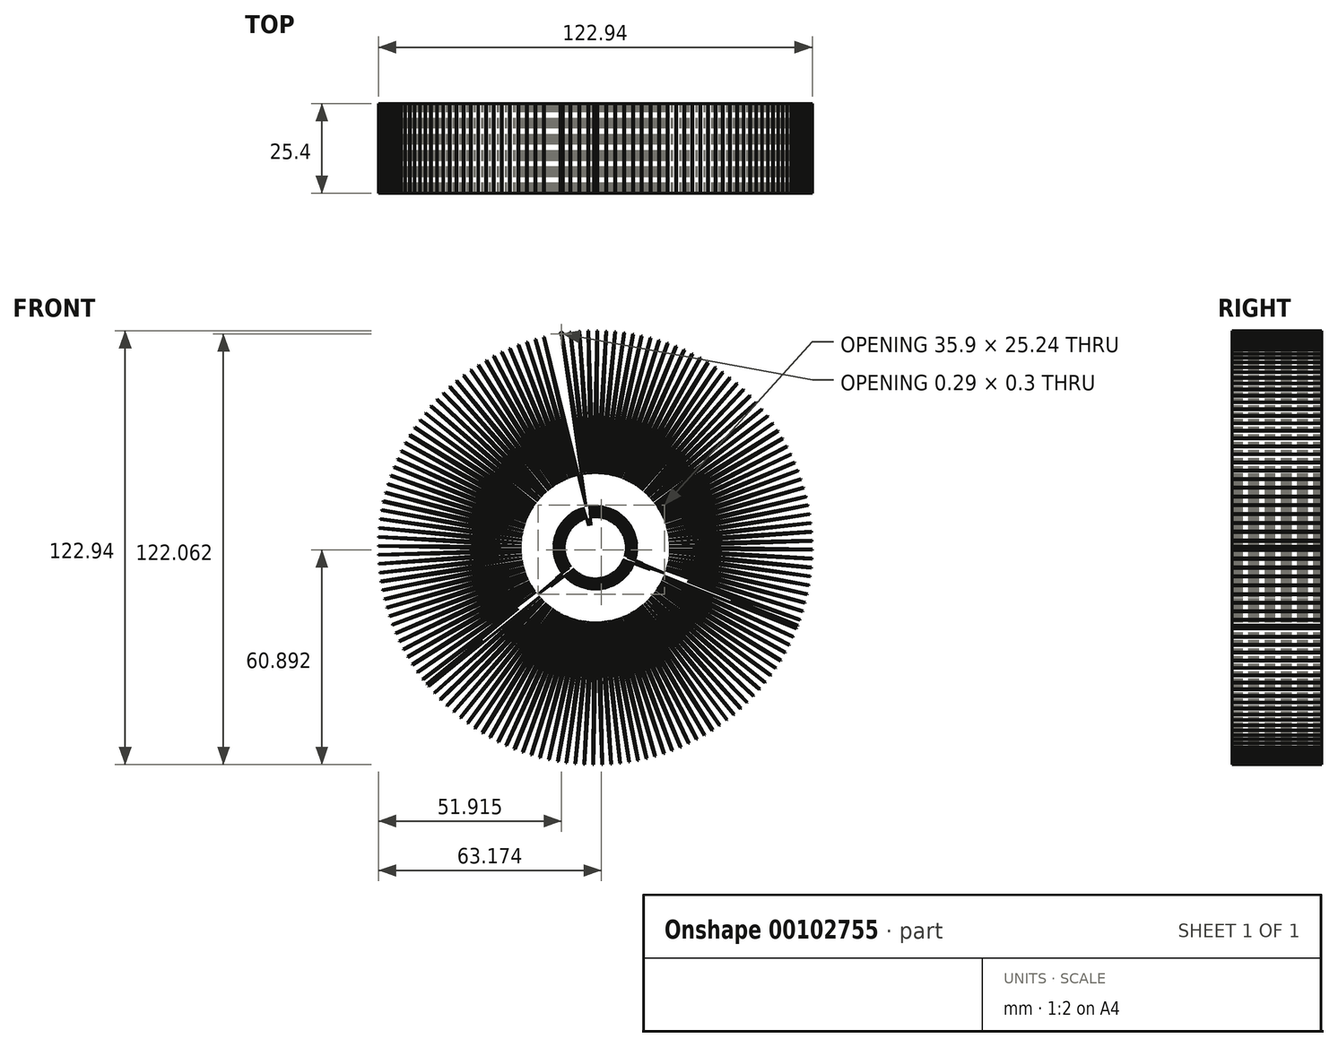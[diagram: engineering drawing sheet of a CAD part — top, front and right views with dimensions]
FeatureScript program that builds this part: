
annotation { "Feature Type Name" : "Feature", "Feature Type Description" : "" }
export const myFeature = defineFeature(function(context is Context, id is Id, definition is map)
    precondition{}
    {
        {
            var Q0;
            Q0=qCreatedBy(makeId("Front.planeOp"),FACE);
            var sketch = newSketch(context, id + "F0", { "sketchPlane" : qUnion([Q0])});
            skCircle(sketch, "E0", {"center": v(0, 0) * mm, "radius": 6.35 * mm});
            skLineSegment(sketch, "E1", {"start": v(-1.78, 6.1) * mm, "end": v(-9.7, 60.7) * mm});
            skLineSegment(sketch, "E2", {"start": v(-9.7, 60.7) * mm, "end": v(-9.43, 60.74) * mm});
            skLineSegment(sketch, "E3", {"start": v(-9.43, 60.74) * mm, "end": v(-0.72, 6.3) * mm});
            skLineSegment(sketch, "E4.1.2.0", {"start": v(-14.68, 59.7) * mm, "end": v(-14.41, 59.75) * mm});
            skLineSegment(sketch, "E4.3.2.0", {"start": v(-2.27, 5.93) * mm, "end": v(-14.68, 59.7) * mm});
            skLineSegment(sketch, "E4.6.2.0", {"start": v(-14.41, 59.75) * mm, "end": v(-1.24, 6.23) * mm});
            skLineSegment(sketch, "E4.1.3.0", {"start": v(-17.13, 59.03) * mm, "end": v(-16.87, 59.1) * mm});
            skLineSegment(sketch, "E4.3.3.0", {"start": v(-2.52, 5.83) * mm, "end": v(-17.13, 59.03) * mm});
            skLineSegment(sketch, "E4.6.3.0", {"start": v(-16.87, 59.1) * mm, "end": v(-1.5, 6.17) * mm});
            skLineSegment(sketch, "E4.1.4.0", {"start": v(-19.56, 58.28) * mm, "end": v(-19.3, 58.36) * mm});
            skLineSegment(sketch, "E4.3.4.0", {"start": v(-2.75, 5.72) * mm, "end": v(-19.56, 58.28) * mm});
            skLineSegment(sketch, "E4.6.4.0", {"start": v(-19.3, 58.36) * mm, "end": v(-1.75, 6.1) * mm});
            skLineSegment(sketch, "E4.1.5.0", {"start": v(-21.95, 57.42) * mm, "end": v(-21.7, 57.51) * mm});
            skLineSegment(sketch, "E4.3.5.0", {"start": v(-2.99, 5.6) * mm, "end": v(-21.95, 57.42) * mm});
            skLineSegment(sketch, "E4.6.5.0", {"start": v(-21.7, 57.51) * mm, "end": v(-2, 6.03) * mm});
            skLineSegment(sketch, "E4.1.6.0", {"start": v(-24.3, 56.46) * mm, "end": v(-24.05, 56.57) * mm});
            skLineSegment(sketch, "E4.3.6.0", {"start": v(-3.22, 5.47) * mm, "end": v(-24.3, 56.46) * mm});
            skLineSegment(sketch, "E4.6.6.0", {"start": v(-24.05, 56.57) * mm, "end": v(-2.24, 5.94) * mm});
            skLineSegment(sketch, "E4.1.7.0", {"start": v(-26.62, 55.4) * mm, "end": v(-26.37, 55.52) * mm});
            skLineSegment(sketch, "E4.3.7.0", {"start": v(-3.44, 5.34) * mm, "end": v(-26.62, 55.4) * mm});
            skLineSegment(sketch, "E4.6.7.0", {"start": v(-26.37, 55.52) * mm, "end": v(-2.49, 5.84) * mm});
            skLineSegment(sketch, "E4.1.8.0", {"start": v(-28.88, 54.26) * mm, "end": v(-28.64, 54.39) * mm});
            skLineSegment(sketch, "E4.3.8.0", {"start": v(-3.66, 5.2) * mm, "end": v(-28.88, 54.26) * mm});
            skLineSegment(sketch, "E4.6.8.0", {"start": v(-28.64, 54.39) * mm, "end": v(-2.73, 5.73) * mm});
            skLineSegment(sketch, "E4.1.9.0", {"start": v(-31.1, 53.02) * mm, "end": v(-30.87, 53.16) * mm});
            skLineSegment(sketch, "E4.3.9.0", {"start": v(-3.87, 5.03) * mm, "end": v(-31.1, 53.02) * mm});
            skLineSegment(sketch, "E4.6.9.0", {"start": v(-30.87, 53.16) * mm, "end": v(-2.96, 5.62) * mm});
            skLineSegment(sketch, "E4.1.10.0", {"start": v(-33.27, 51.7) * mm, "end": v(-33.04, 51.84) * mm});
            skLineSegment(sketch, "E4.3.10.0", {"start": v(-4.07, 4.87) * mm, "end": v(-33.27, 51.7) * mm});
            skLineSegment(sketch, "E4.6.10.0", {"start": v(-33.04, 51.84) * mm, "end": v(-3.2, 5.5) * mm});
            skLineSegment(sketch, "E4.1.11.0", {"start": v(-35.37, 50.27) * mm, "end": v(-35.15, 50.43) * mm});
            skLineSegment(sketch, "E4.3.11.0", {"start": v(-4.27, 4.7) * mm, "end": v(-35.37, 50.27) * mm});
            skLineSegment(sketch, "E4.6.11.0", {"start": v(-35.15, 50.43) * mm, "end": v(-3.41, 5.35) * mm});
            skLineSegment(sketch, "E4.1.12.0", {"start": v(-37.42, 48.77) * mm, "end": v(-37.2, 48.93) * mm});
            skLineSegment(sketch, "E4.3.12.0", {"start": v(-4.46, 4.52) * mm, "end": v(-37.42, 48.77) * mm});
            skLineSegment(sketch, "E4.6.12.0", {"start": v(-37.2, 48.93) * mm, "end": v(-3.63, 5.2) * mm});
            skLineSegment(sketch, "E4.1.13.0", {"start": v(-39.4, 47.18) * mm, "end": v(-39.2, 47.35) * mm});
            skLineSegment(sketch, "E4.3.13.0", {"start": v(-4.65, 4.33) * mm, "end": v(-39.4, 47.18) * mm});
            skLineSegment(sketch, "E4.6.13.0", {"start": v(-39.2, 47.35) * mm, "end": v(-3.85, 5.05) * mm});
            skLineSegment(sketch, "E4.1.14.0", {"start": v(-41.32, 45.51) * mm, "end": v(-41.12, 45.7) * mm});
            skLineSegment(sketch, "E4.3.14.0", {"start": v(-4.82, 4.13) * mm, "end": v(-41.32, 45.51) * mm});
            skLineSegment(sketch, "E4.6.14.0", {"start": v(-41.12, 45.7) * mm, "end": v(-4.05, 4.9) * mm});
            skLineSegment(sketch, "E4.1.15.0", {"start": v(-43.17, 43.76) * mm, "end": v(-42.97, 43.95) * mm});
            skLineSegment(sketch, "E4.3.15.0", {"start": v(-4.99, 3.93) * mm, "end": v(-43.17, 43.76) * mm});
            skLineSegment(sketch, "E4.6.15.0", {"start": v(-42.97, 43.95) * mm, "end": v(-4.25, 4.72) * mm});
            skLineSegment(sketch, "E4.1.16.0", {"start": v(-44.94, 41.94) * mm, "end": v(-44.75, 42.14) * mm});
            skLineSegment(sketch, "E4.3.16.0", {"start": v(-5.15, 3.72) * mm, "end": v(-44.94, 41.94) * mm});
            skLineSegment(sketch, "E4.6.16.0", {"start": v(-44.75, 42.14) * mm, "end": v(-4.44, 4.54) * mm});
            skLineSegment(sketch, "E4.1.17.0", {"start": v(-46.63, 40.05) * mm, "end": v(-46.45, 40.25) * mm});
            skLineSegment(sketch, "E4.3.17.0", {"start": v(-5.3, 3.5) * mm, "end": v(-46.63, 40.05) * mm});
            skLineSegment(sketch, "E4.6.17.0", {"start": v(-46.45, 40.25) * mm, "end": v(-4.62, 4.35) * mm});
            skLineSegment(sketch, "E4.1.18.0", {"start": v(-48.25, 38.09) * mm, "end": v(-48.08, 38.3) * mm});
            skLineSegment(sketch, "E4.3.18.0", {"start": v(-5.44, 3.28) * mm, "end": v(-48.25, 38.09) * mm});
            skLineSegment(sketch, "E4.6.18.0", {"start": v(-48.08, 38.3) * mm, "end": v(-4.8, 4.16) * mm});
            skLineSegment(sketch, "E4.1.19.0", {"start": v(-49.78, 36.06) * mm, "end": v(-49.62, 36.28) * mm});
            skLineSegment(sketch, "E4.3.19.0", {"start": v(-5.57, 3.06) * mm, "end": v(-49.78, 36.06) * mm});
            skLineSegment(sketch, "E4.6.19.0", {"start": v(-49.62, 36.28) * mm, "end": v(-4.97, 3.95) * mm});
            skLineSegment(sketch, "E4.1.20.0", {"start": v(-51.23, 33.97) * mm, "end": v(-51.08, 34.2) * mm});
            skLineSegment(sketch, "E4.3.20.0", {"start": v(-5.69, 2.82) * mm, "end": v(-51.23, 33.97) * mm});
            skLineSegment(sketch, "E4.6.20.0", {"start": v(-51.08, 34.2) * mm, "end": v(-5.13, 3.75) * mm});
            skLineSegment(sketch, "E4.1.21.0", {"start": v(-52.59, 31.83) * mm, "end": v(-52.44, 32.06) * mm});
            skLineSegment(sketch, "E4.3.21.0", {"start": v(-5.8, 2.59) * mm, "end": v(-52.59, 31.83) * mm});
            skLineSegment(sketch, "E4.6.21.0", {"start": v(-52.44, 32.06) * mm, "end": v(-5.28, 3.53) * mm});
            skLineSegment(sketch, "E4.1.22.0", {"start": v(-53.86, 29.63) * mm, "end": v(-53.72, 29.87) * mm});
            skLineSegment(sketch, "E4.3.22.0", {"start": v(-5.9, 2.34) * mm, "end": v(-53.86, 29.63) * mm});
            skLineSegment(sketch, "E4.6.22.0", {"start": v(-53.72, 29.87) * mm, "end": v(-5.42, 3.3) * mm});
            skLineSegment(sketch, "E4.1.23.0", {"start": v(-55.04, 27.38) * mm, "end": v(-54.91, 27.62) * mm});
            skLineSegment(sketch, "E4.3.23.0", {"start": v(-6, 2.1) * mm, "end": v(-55.04, 27.38) * mm});
            skLineSegment(sketch, "E4.6.23.0", {"start": v(-54.91, 27.62) * mm, "end": v(-5.55, 3.08) * mm});
            skLineSegment(sketch, "E4.1.24.0", {"start": v(-56.12, 25.08) * mm, "end": v(-56, 25.33) * mm});
            skLineSegment(sketch, "E4.3.24.0", {"start": v(-6.08, 1.85) * mm, "end": v(-56.12, 25.08) * mm});
            skLineSegment(sketch, "E4.6.24.0", {"start": v(-56, 25.33) * mm, "end": v(-5.67, 2.85) * mm});
            skLineSegment(sketch, "E4.1.25.0", {"start": v(-57.11, 22.74) * mm, "end": v(-57, 23) * mm});
            skLineSegment(sketch, "E4.3.25.0", {"start": v(-6.15, 1.6) * mm, "end": v(-57.11, 22.74) * mm});
            skLineSegment(sketch, "E4.6.25.0", {"start": v(-57, 23) * mm, "end": v(-5.79, 2.61) * mm});
            skLineSegment(sketch, "E4.1.26.0", {"start": v(-58, 20.36) * mm, "end": v(-57.9, 20.61) * mm});
            skLineSegment(sketch, "E4.3.26.0", {"start": v(-6.2, 1.34) * mm, "end": v(-58, 20.36) * mm});
            skLineSegment(sketch, "E4.6.26.0", {"start": v(-57.9, 20.61) * mm, "end": v(-5.9, 2.37) * mm});
            skLineSegment(sketch, "E4.1.27.0", {"start": v(-58.8, 17.95) * mm, "end": v(-58.71, 18.2) * mm});
            skLineSegment(sketch, "E4.3.27.0", {"start": v(-6.26, 1.08) * mm, "end": v(-58.8, 17.95) * mm});
            skLineSegment(sketch, "E4.6.27.0", {"start": v(-58.71, 18.2) * mm, "end": v(-5.98, 2.13) * mm});
            skLineSegment(sketch, "E4.1.28.0", {"start": v(-59.48, 15.5) * mm, "end": v(-59.41, 15.76) * mm});
            skLineSegment(sketch, "E4.3.28.0", {"start": v(-6.3, 0.82) * mm, "end": v(-59.48, 15.5) * mm});
            skLineSegment(sketch, "E4.6.28.0", {"start": v(-59.41, 15.76) * mm, "end": v(-6.07, 1.88) * mm});
            skLineSegment(sketch, "E4.1.29.0", {"start": v(-60.07, 13.03) * mm, "end": v(-60.01, 13.3) * mm});
            skLineSegment(sketch, "E4.3.29.0", {"start": v(-6.33, 0.56) * mm, "end": v(-60.07, 13.03) * mm});
            skLineSegment(sketch, "E4.6.29.0", {"start": v(-60.01, 13.3) * mm, "end": v(-6.14, 1.63) * mm});
            skLineSegment(sketch, "E4.1.30.0", {"start": v(-60.56, 10.53) * mm, "end": v(-60.51, 10.8) * mm});
            skLineSegment(sketch, "E4.3.30.0", {"start": v(-6.34, 0.3) * mm, "end": v(-60.56, 10.53) * mm});
            skLineSegment(sketch, "E4.6.30.0", {"start": v(-60.51, 10.8) * mm, "end": v(-6.2, 1.37) * mm});
            skLineSegment(sketch, "E4.1.31.0", {"start": v(-60.95, 8.02) * mm, "end": v(-60.9, 8.3) * mm});
            skLineSegment(sketch, "E4.3.31.0", {"start": v(-6.35, 0.04) * mm, "end": v(-60.95, 8.02) * mm});
            skLineSegment(sketch, "E4.6.31.0", {"start": v(-60.9, 8.3) * mm, "end": v(-6.25, 1.11) * mm});
            skLineSegment(sketch, "E4.1.32.0", {"start": v(-61.22, 5.5) * mm, "end": v(-61.2, 5.77) * mm});
            skLineSegment(sketch, "E4.3.32.0", {"start": v(-6.35, -0.22) * mm, "end": v(-61.22, 5.5) * mm});
            skLineSegment(sketch, "E4.6.32.0", {"start": v(-61.2, 5.77) * mm, "end": v(-6.3, 0.85) * mm});
            skLineSegment(sketch, "E4.1.33.0", {"start": v(-61.4, 2.96) * mm, "end": v(-61.38, 3.23) * mm});
            skLineSegment(sketch, "E4.3.33.0", {"start": v(-6.33, -0.49) * mm, "end": v(-61.4, 2.96) * mm});
            skLineSegment(sketch, "E4.6.33.0", {"start": v(-61.38, 3.23) * mm, "end": v(-6.32, 0.6) * mm});
            skLineSegment(sketch, "E4.1.34.0", {"start": v(-61.47, 0.42) * mm, "end": v(-61.46, 0.7) * mm});
            skLineSegment(sketch, "E4.3.34.0", {"start": v(-6.3, -0.75) * mm, "end": v(-61.47, 0.42) * mm});
            skLineSegment(sketch, "E4.6.34.0", {"start": v(-61.46, 0.7) * mm, "end": v(-6.34, 0.33) * mm});
            skLineSegment(sketch, "E4.1.35.0", {"start": v(-61.43, -2.12) * mm, "end": v(-61.44, -1.85) * mm});
            skLineSegment(sketch, "E4.3.35.0", {"start": v(-6.27, -1) * mm, "end": v(-61.43, -2.12) * mm});
            skLineSegment(sketch, "E4.6.35.0", {"start": v(-61.44, -1.85) * mm, "end": v(-6.35, 0.07) * mm});
            skLineSegment(sketch, "E4.1.36.0", {"start": v(-61.3, -4.65) * mm, "end": v(-61.31, -4.38) * mm});
            skLineSegment(sketch, "E4.3.36.0", {"start": v(-6.22, -1.27) * mm, "end": v(-61.3, -4.65) * mm});
            skLineSegment(sketch, "E4.6.36.0", {"start": v(-61.31, -4.38) * mm, "end": v(-6.35, -0.2) * mm});
            skLineSegment(sketch, "E4.1.37.0", {"start": v(-61.05, -7.18) * mm, "end": v(-61.08, -6.91) * mm});
            skLineSegment(sketch, "E4.3.37.0", {"start": v(-6.16, -1.52) * mm, "end": v(-61.05, -7.18) * mm});
            skLineSegment(sketch, "E4.6.37.0", {"start": v(-61.08, -6.91) * mm, "end": v(-6.33, -0.46) * mm});
            skLineSegment(sketch, "E4.1.38.0", {"start": v(-60.7, -9.7) * mm, "end": v(-60.74, -9.43) * mm});
            skLineSegment(sketch, "E4.3.38.0", {"start": v(-6.1, -1.78) * mm, "end": v(-60.7, -9.7) * mm});
            skLineSegment(sketch, "E4.6.38.0", {"start": v(-60.74, -9.43) * mm, "end": v(-6.3, -0.72) * mm});
            skLineSegment(sketch, "E4.1.39.0", {"start": v(-60.25, -12.2) * mm, "end": v(-60.3, -11.93) * mm});
            skLineSegment(sketch, "E4.3.39.0", {"start": v(-6.02, -2.03) * mm, "end": v(-60.25, -12.2) * mm});
            skLineSegment(sketch, "E4.6.39.0", {"start": v(-60.3, -11.93) * mm, "end": v(-6.27, -0.98) * mm});
            skLineSegment(sketch, "E4.1.40.0", {"start": v(-59.7, -14.68) * mm, "end": v(-59.75, -14.41) * mm});
            skLineSegment(sketch, "E4.3.40.0", {"start": v(-5.93, -2.27) * mm, "end": v(-59.7, -14.68) * mm});
            skLineSegment(sketch, "E4.6.40.0", {"start": v(-59.75, -14.41) * mm, "end": v(-6.23, -1.24) * mm});
            skLineSegment(sketch, "E4.1.41.0", {"start": v(-59.03, -17.13) * mm, "end": v(-59.1, -16.87) * mm});
            skLineSegment(sketch, "E4.3.41.0", {"start": v(-5.83, -2.52) * mm, "end": v(-59.03, -17.13) * mm});
            skLineSegment(sketch, "E4.6.41.0", {"start": v(-59.1, -16.87) * mm, "end": v(-6.17, -1.5) * mm});
            skLineSegment(sketch, "E4.1.42.0", {"start": v(-58.28, -19.56) * mm, "end": v(-58.36, -19.3) * mm});
            skLineSegment(sketch, "E4.3.42.0", {"start": v(-5.72, -2.75) * mm, "end": v(-58.28, -19.56) * mm});
            skLineSegment(sketch, "E4.6.42.0", {"start": v(-58.36, -19.3) * mm, "end": v(-6.1, -1.75) * mm});
            skLineSegment(sketch, "E4.1.43.0", {"start": v(-57.42, -21.95) * mm, "end": v(-57.51, -21.7) * mm});
            skLineSegment(sketch, "E4.3.43.0", {"start": v(-5.6, -2.99) * mm, "end": v(-57.42, -21.95) * mm});
            skLineSegment(sketch, "E4.6.43.0", {"start": v(-57.51, -21.7) * mm, "end": v(-6.03, -2) * mm});
            skLineSegment(sketch, "E4.1.44.0", {"start": v(-56.46, -24.3) * mm, "end": v(-56.57, -24.05) * mm});
            skLineSegment(sketch, "E4.3.44.0", {"start": v(-5.47, -3.22) * mm, "end": v(-56.46, -24.3) * mm});
            skLineSegment(sketch, "E4.6.44.0", {"start": v(-56.57, -24.05) * mm, "end": v(-5.94, -2.24) * mm});
            skLineSegment(sketch, "E4.1.45.0", {"start": v(-55.4, -26.62) * mm, "end": v(-55.52, -26.37) * mm});
            skLineSegment(sketch, "E4.3.45.0", {"start": v(-5.34, -3.44) * mm, "end": v(-55.4, -26.62) * mm});
            skLineSegment(sketch, "E4.6.45.0", {"start": v(-55.52, -26.37) * mm, "end": v(-5.84, -2.49) * mm});
            skLineSegment(sketch, "E4.1.46.0", {"start": v(-54.26, -28.88) * mm, "end": v(-54.39, -28.64) * mm});
            skLineSegment(sketch, "E4.3.46.0", {"start": v(-5.2, -3.66) * mm, "end": v(-54.26, -28.88) * mm});
            skLineSegment(sketch, "E4.6.46.0", {"start": v(-54.39, -28.64) * mm, "end": v(-5.73, -2.73) * mm});
            skLineSegment(sketch, "E4.1.47.0", {"start": v(-53.02, -31.1) * mm, "end": v(-53.16, -30.87) * mm});
            skLineSegment(sketch, "E4.3.47.0", {"start": v(-5.03, -3.87) * mm, "end": v(-53.02, -31.1) * mm});
            skLineSegment(sketch, "E4.6.47.0", {"start": v(-53.16, -30.87) * mm, "end": v(-5.62, -2.96) * mm});
            skLineSegment(sketch, "E4.1.48.0", {"start": v(-51.7, -33.27) * mm, "end": v(-51.84, -33.04) * mm});
            skLineSegment(sketch, "E4.3.48.0", {"start": v(-4.87, -4.07) * mm, "end": v(-51.7, -33.27) * mm});
            skLineSegment(sketch, "E4.6.48.0", {"start": v(-51.84, -33.04) * mm, "end": v(-5.5, -3.2) * mm});
            skLineSegment(sketch, "E4.1.49.0", {"start": v(-50.27, -35.37) * mm, "end": v(-50.43, -35.15) * mm});
            skLineSegment(sketch, "E4.3.49.0", {"start": v(-4.7, -4.27) * mm, "end": v(-50.27, -35.37) * mm});
            skLineSegment(sketch, "E4.6.49.0", {"start": v(-50.43, -35.15) * mm, "end": v(-5.35, -3.41) * mm});
            skLineSegment(sketch, "E4.1.50.0", {"start": v(-48.77, -37.42) * mm, "end": v(-48.93, -37.2) * mm});
            skLineSegment(sketch, "E4.3.50.0", {"start": v(-4.52, -4.46) * mm, "end": v(-48.77, -37.42) * mm});
            skLineSegment(sketch, "E4.6.50.0", {"start": v(-48.93, -37.2) * mm, "end": v(-5.2, -3.63) * mm});
            skLineSegment(sketch, "E4.1.51.0", {"start": v(-47.18, -39.4) * mm, "end": v(-47.35, -39.2) * mm});
            skLineSegment(sketch, "E4.3.51.0", {"start": v(-4.33, -4.65) * mm, "end": v(-47.18, -39.4) * mm});
            skLineSegment(sketch, "E4.6.51.0", {"start": v(-47.35, -39.2) * mm, "end": v(-5.05, -3.85) * mm});
            skLineSegment(sketch, "E4.1.52.0", {"start": v(-45.51, -41.32) * mm, "end": v(-45.7, -41.12) * mm});
            skLineSegment(sketch, "E4.3.52.0", {"start": v(-4.13, -4.82) * mm, "end": v(-45.51, -41.32) * mm});
            skLineSegment(sketch, "E4.6.52.0", {"start": v(-45.7, -41.12) * mm, "end": v(-4.9, -4.05) * mm});
            skLineSegment(sketch, "E4.1.53.0", {"start": v(-43.76, -43.17) * mm, "end": v(-43.95, -42.97) * mm});
            skLineSegment(sketch, "E4.3.53.0", {"start": v(-3.93, -4.99) * mm, "end": v(-43.76, -43.17) * mm});
            skLineSegment(sketch, "E4.6.53.0", {"start": v(-43.95, -42.97) * mm, "end": v(-4.72, -4.25) * mm});
            skLineSegment(sketch, "E4.1.54.0", {"start": v(-41.94, -44.94) * mm, "end": v(-42.14, -44.75) * mm});
            skLineSegment(sketch, "E4.3.54.0", {"start": v(-3.72, -5.15) * mm, "end": v(-41.94, -44.94) * mm});
            skLineSegment(sketch, "E4.6.54.0", {"start": v(-42.14, -44.75) * mm, "end": v(-4.54, -4.44) * mm});
            skLineSegment(sketch, "E4.1.55.0", {"start": v(-40.05, -46.63) * mm, "end": v(-40.25, -46.45) * mm});
            skLineSegment(sketch, "E4.3.55.0", {"start": v(-3.5, -5.3) * mm, "end": v(-40.05, -46.63) * mm});
            skLineSegment(sketch, "E4.6.55.0", {"start": v(-40.25, -46.45) * mm, "end": v(-4.35, -4.62) * mm});
            skLineSegment(sketch, "E4.1.56.0", {"start": v(-38.09, -48.25) * mm, "end": v(-38.3, -48.08) * mm});
            skLineSegment(sketch, "E4.3.56.0", {"start": v(-3.28, -5.44) * mm, "end": v(-38.09, -48.25) * mm});
            skLineSegment(sketch, "E4.6.56.0", {"start": v(-38.3, -48.08) * mm, "end": v(-4.16, -4.8) * mm});
            skLineSegment(sketch, "E4.1.57.0", {"start": v(-36.06, -49.78) * mm, "end": v(-36.28, -49.62) * mm});
            skLineSegment(sketch, "E4.3.57.0", {"start": v(-3.06, -5.57) * mm, "end": v(-36.06, -49.78) * mm});
            skLineSegment(sketch, "E4.6.57.0", {"start": v(-36.28, -49.62) * mm, "end": v(-3.95, -4.97) * mm});
            skLineSegment(sketch, "E4.1.58.0", {"start": v(-33.97, -51.23) * mm, "end": v(-34.2, -51.08) * mm});
            skLineSegment(sketch, "E4.3.58.0", {"start": v(-2.82, -5.69) * mm, "end": v(-33.97, -51.23) * mm});
            skLineSegment(sketch, "E4.6.58.0", {"start": v(-34.2, -51.08) * mm, "end": v(-3.75, -5.13) * mm});
            skLineSegment(sketch, "E4.1.59.0", {"start": v(-31.83, -52.59) * mm, "end": v(-32.06, -52.44) * mm});
            skLineSegment(sketch, "E4.3.59.0", {"start": v(-2.59, -5.8) * mm, "end": v(-31.83, -52.59) * mm});
            skLineSegment(sketch, "E4.6.59.0", {"start": v(-32.06, -52.44) * mm, "end": v(-3.53, -5.28) * mm});
            skLineSegment(sketch, "E4.1.60.0", {"start": v(-29.63, -53.86) * mm, "end": v(-29.87, -53.72) * mm});
            skLineSegment(sketch, "E4.3.60.0", {"start": v(-2.34, -5.9) * mm, "end": v(-29.63, -53.86) * mm});
            skLineSegment(sketch, "E4.6.60.0", {"start": v(-29.87, -53.72) * mm, "end": v(-3.3, -5.42) * mm});
            skLineSegment(sketch, "E4.1.61.0", {"start": v(-27.38, -55.04) * mm, "end": v(-27.62, -54.91) * mm});
            skLineSegment(sketch, "E4.3.61.0", {"start": v(-2.1, -6) * mm, "end": v(-27.38, -55.04) * mm});
            skLineSegment(sketch, "E4.6.61.0", {"start": v(-27.62, -54.91) * mm, "end": v(-3.08, -5.55) * mm});
            skLineSegment(sketch, "E4.1.62.0", {"start": v(-25.08, -56.12) * mm, "end": v(-25.33, -56) * mm});
            skLineSegment(sketch, "E4.3.62.0", {"start": v(-1.85, -6.08) * mm, "end": v(-25.08, -56.12) * mm});
            skLineSegment(sketch, "E4.6.62.0", {"start": v(-25.33, -56) * mm, "end": v(-2.85, -5.67) * mm});
            skLineSegment(sketch, "E4.1.63.0", {"start": v(-22.74, -57.11) * mm, "end": v(-23, -57) * mm});
            skLineSegment(sketch, "E4.3.63.0", {"start": v(-1.6, -6.15) * mm, "end": v(-22.74, -57.11) * mm});
            skLineSegment(sketch, "E4.6.63.0", {"start": v(-23, -57) * mm, "end": v(-2.61, -5.79) * mm});
            skLineSegment(sketch, "E4.1.64.0", {"start": v(-20.36, -58) * mm, "end": v(-20.61, -57.9) * mm});
            skLineSegment(sketch, "E4.3.64.0", {"start": v(-1.34, -6.2) * mm, "end": v(-20.36, -58) * mm});
            skLineSegment(sketch, "E4.6.64.0", {"start": v(-20.61, -57.9) * mm, "end": v(-2.37, -5.9) * mm});
            skLineSegment(sketch, "E4.1.65.0", {"start": v(-17.95, -58.8) * mm, "end": v(-18.2, -58.71) * mm});
            skLineSegment(sketch, "E4.3.65.0", {"start": v(-1.08, -6.26) * mm, "end": v(-17.95, -58.8) * mm});
            skLineSegment(sketch, "E4.6.65.0", {"start": v(-18.2, -58.71) * mm, "end": v(-2.13, -5.98) * mm});
            skLineSegment(sketch, "E4.1.66.0", {"start": v(-15.5, -59.48) * mm, "end": v(-15.76, -59.41) * mm});
            skLineSegment(sketch, "E4.3.66.0", {"start": v(-0.82, -6.3) * mm, "end": v(-15.5, -59.48) * mm});
            skLineSegment(sketch, "E4.6.66.0", {"start": v(-15.76, -59.41) * mm, "end": v(-1.88, -6.07) * mm});
            skLineSegment(sketch, "E4.1.67.0", {"start": v(-13.03, -60.07) * mm, "end": v(-13.3, -60.01) * mm});
            skLineSegment(sketch, "E4.3.67.0", {"start": v(-0.56, -6.33) * mm, "end": v(-13.03, -60.07) * mm});
            skLineSegment(sketch, "E4.6.67.0", {"start": v(-13.3, -60.01) * mm, "end": v(-1.63, -6.14) * mm});
            skLineSegment(sketch, "E4.1.68.0", {"start": v(-10.53, -60.56) * mm, "end": v(-10.8, -60.51) * mm});
            skLineSegment(sketch, "E4.3.68.0", {"start": v(-0.3, -6.34) * mm, "end": v(-10.53, -60.56) * mm});
            skLineSegment(sketch, "E4.6.68.0", {"start": v(-10.8, -60.51) * mm, "end": v(-1.37, -6.2) * mm});
            skLineSegment(sketch, "E4.1.69.0", {"start": v(-8.02, -60.95) * mm, "end": v(-8.3, -60.9) * mm});
            skLineSegment(sketch, "E4.3.69.0", {"start": v(-0.04, -6.35) * mm, "end": v(-8.02, -60.95) * mm});
            skLineSegment(sketch, "E4.6.69.0", {"start": v(-8.3, -60.9) * mm, "end": v(-1.11, -6.25) * mm});
            skLineSegment(sketch, "E4.1.70.0", {"start": v(-5.5, -61.22) * mm, "end": v(-5.77, -61.2) * mm});
            skLineSegment(sketch, "E4.3.70.0", {"start": v(0.22, -6.35) * mm, "end": v(-5.5, -61.22) * mm});
            skLineSegment(sketch, "E4.6.70.0", {"start": v(-5.77, -61.2) * mm, "end": v(-0.85, -6.3) * mm});
            skLineSegment(sketch, "E4.1.71.0", {"start": v(-2.96, -61.4) * mm, "end": v(-3.23, -61.38) * mm});
            skLineSegment(sketch, "E4.3.71.0", {"start": v(0.49, -6.33) * mm, "end": v(-2.96, -61.4) * mm});
            skLineSegment(sketch, "E4.6.71.0", {"start": v(-3.23, -61.38) * mm, "end": v(-0.6, -6.32) * mm});
            skLineSegment(sketch, "E4.1.72.0", {"start": v(-0.42, -61.47) * mm, "end": v(-0.7, -61.46) * mm});
            skLineSegment(sketch, "E4.3.72.0", {"start": v(0.75, -6.3) * mm, "end": v(-0.42, -61.47) * mm});
            skLineSegment(sketch, "E4.6.72.0", {"start": v(-0.7, -61.46) * mm, "end": v(-0.33, -6.34) * mm});
            skLineSegment(sketch, "E4.1.73.0", {"start": v(2.12, -61.43) * mm, "end": v(1.85, -61.44) * mm});
            skLineSegment(sketch, "E4.3.73.0", {"start": v(1, -6.27) * mm, "end": v(2.12, -61.43) * mm});
            skLineSegment(sketch, "E4.6.73.0", {"start": v(1.85, -61.44) * mm, "end": v(-0.07, -6.35) * mm});
            skLineSegment(sketch, "E4.1.74.0", {"start": v(4.65, -61.3) * mm, "end": v(4.38, -61.31) * mm});
            skLineSegment(sketch, "E4.3.74.0", {"start": v(1.27, -6.22) * mm, "end": v(4.65, -61.3) * mm});
            skLineSegment(sketch, "E4.6.74.0", {"start": v(4.38, -61.31) * mm, "end": v(0.2, -6.35) * mm});
            skLineSegment(sketch, "E4.1.75.0", {"start": v(7.18, -61.05) * mm, "end": v(6.91, -61.08) * mm});
            skLineSegment(sketch, "E4.3.75.0", {"start": v(1.52, -6.16) * mm, "end": v(7.18, -61.05) * mm});
            skLineSegment(sketch, "E4.6.75.0", {"start": v(6.91, -61.08) * mm, "end": v(0.46, -6.33) * mm});
            skLineSegment(sketch, "E4.1.76.0", {"start": v(9.7, -60.7) * mm, "end": v(9.43, -60.74) * mm});
            skLineSegment(sketch, "E4.3.76.0", {"start": v(1.78, -6.1) * mm, "end": v(9.7, -60.7) * mm});
            skLineSegment(sketch, "E4.6.76.0", {"start": v(9.43, -60.74) * mm, "end": v(0.72, -6.3) * mm});
            skLineSegment(sketch, "E4.1.77.0", {"start": v(12.2, -60.25) * mm, "end": v(11.93, -60.3) * mm});
            skLineSegment(sketch, "E4.3.77.0", {"start": v(2.03, -6.02) * mm, "end": v(12.2, -60.25) * mm});
            skLineSegment(sketch, "E4.6.77.0", {"start": v(11.93, -60.3) * mm, "end": v(0.98, -6.27) * mm});
            skLineSegment(sketch, "E4.1.78.0", {"start": v(14.68, -59.7) * mm, "end": v(14.41, -59.75) * mm});
            skLineSegment(sketch, "E4.3.78.0", {"start": v(2.27, -5.93) * mm, "end": v(14.68, -59.7) * mm});
            skLineSegment(sketch, "E4.6.78.0", {"start": v(14.41, -59.75) * mm, "end": v(1.24, -6.23) * mm});
            skLineSegment(sketch, "E4.1.79.0", {"start": v(17.13, -59.03) * mm, "end": v(16.87, -59.1) * mm});
            skLineSegment(sketch, "E4.3.79.0", {"start": v(2.52, -5.83) * mm, "end": v(17.13, -59.03) * mm});
            skLineSegment(sketch, "E4.6.79.0", {"start": v(16.87, -59.1) * mm, "end": v(1.5, -6.17) * mm});
            skLineSegment(sketch, "E4.1.80.0", {"start": v(19.56, -58.28) * mm, "end": v(19.3, -58.36) * mm});
            skLineSegment(sketch, "E4.3.80.0", {"start": v(2.75, -5.72) * mm, "end": v(19.56, -58.28) * mm});
            skLineSegment(sketch, "E4.6.80.0", {"start": v(19.3, -58.36) * mm, "end": v(1.75, -6.1) * mm});
            skLineSegment(sketch, "E4.1.81.0", {"start": v(21.95, -57.42) * mm, "end": v(21.7, -57.51) * mm});
            skLineSegment(sketch, "E4.3.81.0", {"start": v(2.99, -5.6) * mm, "end": v(21.95, -57.42) * mm});
            skLineSegment(sketch, "E4.6.81.0", {"start": v(21.7, -57.51) * mm, "end": v(2, -6.03) * mm});
            skLineSegment(sketch, "E4.1.82.0", {"start": v(24.3, -56.46) * mm, "end": v(24.05, -56.57) * mm});
            skLineSegment(sketch, "E4.3.82.0", {"start": v(3.22, -5.47) * mm, "end": v(24.3, -56.46) * mm});
            skLineSegment(sketch, "E4.6.82.0", {"start": v(24.05, -56.57) * mm, "end": v(2.24, -5.94) * mm});
            skLineSegment(sketch, "E4.1.83.0", {"start": v(26.62, -55.4) * mm, "end": v(26.37, -55.52) * mm});
            skLineSegment(sketch, "E4.3.83.0", {"start": v(3.44, -5.34) * mm, "end": v(26.62, -55.4) * mm});
            skLineSegment(sketch, "E4.6.83.0", {"start": v(26.37, -55.52) * mm, "end": v(2.49, -5.84) * mm});
            skLineSegment(sketch, "E4.1.84.0", {"start": v(28.88, -54.26) * mm, "end": v(28.64, -54.39) * mm});
            skLineSegment(sketch, "E4.3.84.0", {"start": v(3.66, -5.2) * mm, "end": v(28.88, -54.26) * mm});
            skLineSegment(sketch, "E4.6.84.0", {"start": v(28.64, -54.39) * mm, "end": v(2.73, -5.73) * mm});
            skLineSegment(sketch, "E4.1.85.0", {"start": v(31.1, -53.02) * mm, "end": v(30.87, -53.16) * mm});
            skLineSegment(sketch, "E4.3.85.0", {"start": v(3.87, -5.03) * mm, "end": v(31.1, -53.02) * mm});
            skLineSegment(sketch, "E4.6.85.0", {"start": v(30.87, -53.16) * mm, "end": v(2.96, -5.62) * mm});
            skLineSegment(sketch, "E4.1.86.0", {"start": v(33.27, -51.7) * mm, "end": v(33.04, -51.84) * mm});
            skLineSegment(sketch, "E4.3.86.0", {"start": v(4.07, -4.87) * mm, "end": v(33.27, -51.7) * mm});
            skLineSegment(sketch, "E4.6.86.0", {"start": v(33.04, -51.84) * mm, "end": v(3.2, -5.5) * mm});
            skLineSegment(sketch, "E4.1.87.0", {"start": v(35.37, -50.27) * mm, "end": v(35.15, -50.43) * mm});
            skLineSegment(sketch, "E4.3.87.0", {"start": v(4.27, -4.7) * mm, "end": v(35.37, -50.27) * mm});
            skLineSegment(sketch, "E4.6.87.0", {"start": v(35.15, -50.43) * mm, "end": v(3.41, -5.35) * mm});
            skLineSegment(sketch, "E4.1.88.0", {"start": v(37.42, -48.77) * mm, "end": v(37.2, -48.93) * mm});
            skLineSegment(sketch, "E4.3.88.0", {"start": v(4.46, -4.52) * mm, "end": v(37.42, -48.77) * mm});
            skLineSegment(sketch, "E4.6.88.0", {"start": v(37.2, -48.93) * mm, "end": v(3.63, -5.2) * mm});
            skLineSegment(sketch, "E4.1.89.0", {"start": v(39.4, -47.18) * mm, "end": v(39.2, -47.35) * mm});
            skLineSegment(sketch, "E4.3.89.0", {"start": v(4.65, -4.33) * mm, "end": v(39.4, -47.18) * mm});
            skLineSegment(sketch, "E4.6.89.0", {"start": v(39.2, -47.35) * mm, "end": v(3.85, -5.05) * mm});
            skLineSegment(sketch, "E4.1.90.0", {"start": v(41.32, -45.51) * mm, "end": v(41.12, -45.7) * mm});
            skLineSegment(sketch, "E4.3.90.0", {"start": v(4.82, -4.13) * mm, "end": v(41.32, -45.51) * mm});
            skLineSegment(sketch, "E4.6.90.0", {"start": v(41.12, -45.7) * mm, "end": v(4.05, -4.9) * mm});
            skLineSegment(sketch, "E4.1.91.0", {"start": v(43.17, -43.76) * mm, "end": v(42.97, -43.95) * mm});
            skLineSegment(sketch, "E4.3.91.0", {"start": v(4.99, -3.93) * mm, "end": v(43.17, -43.76) * mm});
            skLineSegment(sketch, "E4.6.91.0", {"start": v(42.97, -43.95) * mm, "end": v(4.25, -4.72) * mm});
            skLineSegment(sketch, "E4.1.92.0", {"start": v(44.94, -41.94) * mm, "end": v(44.75, -42.14) * mm});
            skLineSegment(sketch, "E4.3.92.0", {"start": v(5.15, -3.72) * mm, "end": v(44.94, -41.94) * mm});
            skLineSegment(sketch, "E4.6.92.0", {"start": v(44.75, -42.14) * mm, "end": v(4.44, -4.54) * mm});
            skLineSegment(sketch, "E4.1.93.0", {"start": v(46.63, -40.05) * mm, "end": v(46.45, -40.25) * mm});
            skLineSegment(sketch, "E4.3.93.0", {"start": v(5.3, -3.5) * mm, "end": v(46.63, -40.05) * mm});
            skLineSegment(sketch, "E4.6.93.0", {"start": v(46.45, -40.25) * mm, "end": v(4.62, -4.35) * mm});
            skLineSegment(sketch, "E4.1.94.0", {"start": v(48.25, -38.09) * mm, "end": v(48.08, -38.3) * mm});
            skLineSegment(sketch, "E4.3.94.0", {"start": v(5.44, -3.28) * mm, "end": v(48.25, -38.09) * mm});
            skLineSegment(sketch, "E4.6.94.0", {"start": v(48.08, -38.3) * mm, "end": v(4.8, -4.16) * mm});
            skLineSegment(sketch, "E4.1.95.0", {"start": v(49.78, -36.06) * mm, "end": v(49.62, -36.28) * mm});
            skLineSegment(sketch, "E4.3.95.0", {"start": v(5.57, -3.06) * mm, "end": v(49.78, -36.06) * mm});
            skLineSegment(sketch, "E4.6.95.0", {"start": v(49.62, -36.28) * mm, "end": v(4.97, -3.95) * mm});
            skLineSegment(sketch, "E4.1.96.0", {"start": v(51.23, -33.97) * mm, "end": v(51.08, -34.2) * mm});
            skLineSegment(sketch, "E4.3.96.0", {"start": v(5.69, -2.82) * mm, "end": v(51.23, -33.97) * mm});
            skLineSegment(sketch, "E4.6.96.0", {"start": v(51.08, -34.2) * mm, "end": v(5.13, -3.75) * mm});
            skLineSegment(sketch, "E4.1.97.0", {"start": v(52.59, -31.83) * mm, "end": v(52.44, -32.06) * mm});
            skLineSegment(sketch, "E4.3.97.0", {"start": v(5.8, -2.59) * mm, "end": v(52.59, -31.83) * mm});
            skLineSegment(sketch, "E4.6.97.0", {"start": v(52.44, -32.06) * mm, "end": v(5.28, -3.53) * mm});
            skLineSegment(sketch, "E4.1.98.0", {"start": v(53.86, -29.63) * mm, "end": v(53.72, -29.87) * mm});
            skLineSegment(sketch, "E4.3.98.0", {"start": v(5.9, -2.34) * mm, "end": v(53.86, -29.63) * mm});
            skLineSegment(sketch, "E4.6.98.0", {"start": v(53.72, -29.87) * mm, "end": v(5.42, -3.3) * mm});
            skLineSegment(sketch, "E4.1.99.0", {"start": v(55.04, -27.38) * mm, "end": v(54.91, -27.62) * mm});
            skLineSegment(sketch, "E4.3.99.0", {"start": v(6, -2.1) * mm, "end": v(55.04, -27.38) * mm});
            skLineSegment(sketch, "E4.6.99.0", {"start": v(54.91, -27.62) * mm, "end": v(5.55, -3.08) * mm});
            skLineSegment(sketch, "E4.1.100.0", {"start": v(56.12, -25.08) * mm, "end": v(56, -25.33) * mm});
            skLineSegment(sketch, "E4.3.100.0", {"start": v(6.08, -1.85) * mm, "end": v(56.12, -25.08) * mm});
            skLineSegment(sketch, "E4.6.100.0", {"start": v(56, -25.33) * mm, "end": v(5.67, -2.85) * mm});
            skLineSegment(sketch, "E4.1.101.0", {"start": v(57.11, -22.74) * mm, "end": v(57, -23) * mm});
            skLineSegment(sketch, "E4.3.101.0", {"start": v(6.15, -1.6) * mm, "end": v(57.11, -22.74) * mm});
            skLineSegment(sketch, "E4.6.101.0", {"start": v(57, -23) * mm, "end": v(5.79, -2.61) * mm});
            skLineSegment(sketch, "E4.1.102.0", {"start": v(58, -20.36) * mm, "end": v(57.9, -20.61) * mm});
            skLineSegment(sketch, "E4.3.102.0", {"start": v(6.2, -1.34) * mm, "end": v(58, -20.36) * mm});
            skLineSegment(sketch, "E4.6.102.0", {"start": v(57.9, -20.61) * mm, "end": v(5.9, -2.37) * mm});
            skLineSegment(sketch, "E4.1.103.0", {"start": v(58.8, -17.95) * mm, "end": v(58.71, -18.2) * mm});
            skLineSegment(sketch, "E4.3.103.0", {"start": v(6.26, -1.08) * mm, "end": v(58.8, -17.95) * mm});
            skLineSegment(sketch, "E4.6.103.0", {"start": v(58.71, -18.2) * mm, "end": v(5.98, -2.13) * mm});
            skLineSegment(sketch, "E4.1.104.0", {"start": v(59.48, -15.5) * mm, "end": v(59.41, -15.76) * mm});
            skLineSegment(sketch, "E4.3.104.0", {"start": v(6.3, -0.82) * mm, "end": v(59.48, -15.5) * mm});
            skLineSegment(sketch, "E4.6.104.0", {"start": v(59.41, -15.76) * mm, "end": v(6.07, -1.88) * mm});
            skLineSegment(sketch, "E4.1.105.0", {"start": v(60.07, -13.03) * mm, "end": v(60.01, -13.3) * mm});
            skLineSegment(sketch, "E4.3.105.0", {"start": v(6.33, -0.56) * mm, "end": v(60.07, -13.03) * mm});
            skLineSegment(sketch, "E4.6.105.0", {"start": v(60.01, -13.3) * mm, "end": v(6.14, -1.63) * mm});
            skLineSegment(sketch, "E4.1.106.0", {"start": v(60.56, -10.53) * mm, "end": v(60.51, -10.8) * mm});
            skLineSegment(sketch, "E4.3.106.0", {"start": v(6.34, -0.3) * mm, "end": v(60.56, -10.53) * mm});
            skLineSegment(sketch, "E4.6.106.0", {"start": v(60.51, -10.8) * mm, "end": v(6.2, -1.37) * mm});
            skLineSegment(sketch, "E4.1.107.0", {"start": v(60.95, -8.02) * mm, "end": v(60.9, -8.3) * mm});
            skLineSegment(sketch, "E4.3.107.0", {"start": v(6.35, -0.04) * mm, "end": v(60.95, -8.02) * mm});
            skLineSegment(sketch, "E4.6.107.0", {"start": v(60.9, -8.3) * mm, "end": v(6.25, -1.11) * mm});
            skLineSegment(sketch, "E4.1.108.0", {"start": v(61.22, -5.5) * mm, "end": v(61.2, -5.77) * mm});
            skLineSegment(sketch, "E4.3.108.0", {"start": v(6.35, 0.22) * mm, "end": v(61.22, -5.5) * mm});
            skLineSegment(sketch, "E4.6.108.0", {"start": v(61.2, -5.77) * mm, "end": v(6.3, -0.85) * mm});
            skLineSegment(sketch, "E4.1.109.0", {"start": v(61.4, -2.96) * mm, "end": v(61.38, -3.23) * mm});
            skLineSegment(sketch, "E4.3.109.0", {"start": v(6.33, 0.49) * mm, "end": v(61.4, -2.96) * mm});
            skLineSegment(sketch, "E4.6.109.0", {"start": v(61.38, -3.23) * mm, "end": v(6.32, -0.6) * mm});
            skLineSegment(sketch, "E4.1.110.0", {"start": v(61.47, -0.42) * mm, "end": v(61.46, -0.7) * mm});
            skLineSegment(sketch, "E4.3.110.0", {"start": v(6.3, 0.75) * mm, "end": v(61.47, -0.42) * mm});
            skLineSegment(sketch, "E4.6.110.0", {"start": v(61.46, -0.7) * mm, "end": v(6.34, -0.33) * mm});
            skLineSegment(sketch, "E4.1.111.0", {"start": v(61.43, 2.12) * mm, "end": v(61.44, 1.85) * mm});
            skLineSegment(sketch, "E4.3.111.0", {"start": v(6.27, 1) * mm, "end": v(61.43, 2.12) * mm});
            skLineSegment(sketch, "E4.6.111.0", {"start": v(61.44, 1.85) * mm, "end": v(6.35, -0.07) * mm});
            skLineSegment(sketch, "E4.1.112.0", {"start": v(61.3, 4.65) * mm, "end": v(61.31, 4.38) * mm});
            skLineSegment(sketch, "E4.3.112.0", {"start": v(6.22, 1.27) * mm, "end": v(61.3, 4.65) * mm});
            skLineSegment(sketch, "E4.6.112.0", {"start": v(61.31, 4.38) * mm, "end": v(6.35, 0.2) * mm});
            skLineSegment(sketch, "E4.1.113.0", {"start": v(61.05, 7.18) * mm, "end": v(61.08, 6.91) * mm});
            skLineSegment(sketch, "E4.3.113.0", {"start": v(6.16, 1.52) * mm, "end": v(61.05, 7.18) * mm});
            skLineSegment(sketch, "E4.6.113.0", {"start": v(61.08, 6.91) * mm, "end": v(6.33, 0.46) * mm});
            skLineSegment(sketch, "E4.1.114.0", {"start": v(60.7, 9.7) * mm, "end": v(60.74, 9.43) * mm});
            skLineSegment(sketch, "E4.3.114.0", {"start": v(6.1, 1.78) * mm, "end": v(60.7, 9.7) * mm});
            skLineSegment(sketch, "E4.6.114.0", {"start": v(60.74, 9.43) * mm, "end": v(6.3, 0.72) * mm});
            skLineSegment(sketch, "E4.1.115.0", {"start": v(60.25, 12.2) * mm, "end": v(60.3, 11.93) * mm});
            skLineSegment(sketch, "E4.3.115.0", {"start": v(6.02, 2.03) * mm, "end": v(60.25, 12.2) * mm});
            skLineSegment(sketch, "E4.6.115.0", {"start": v(60.3, 11.93) * mm, "end": v(6.27, 0.98) * mm});
            skLineSegment(sketch, "E4.1.116.0", {"start": v(59.7, 14.68) * mm, "end": v(59.75, 14.41) * mm});
            skLineSegment(sketch, "E4.3.116.0", {"start": v(5.93, 2.27) * mm, "end": v(59.7, 14.68) * mm});
            skLineSegment(sketch, "E4.6.116.0", {"start": v(59.75, 14.41) * mm, "end": v(6.23, 1.24) * mm});
            skLineSegment(sketch, "E4.1.117.0", {"start": v(59.03, 17.13) * mm, "end": v(59.1, 16.87) * mm});
            skLineSegment(sketch, "E4.3.117.0", {"start": v(5.83, 2.52) * mm, "end": v(59.03, 17.13) * mm});
            skLineSegment(sketch, "E4.6.117.0", {"start": v(59.1, 16.87) * mm, "end": v(6.17, 1.5) * mm});
            skLineSegment(sketch, "E4.1.118.0", {"start": v(58.28, 19.56) * mm, "end": v(58.36, 19.3) * mm});
            skLineSegment(sketch, "E4.3.118.0", {"start": v(5.72, 2.75) * mm, "end": v(58.28, 19.56) * mm});
            skLineSegment(sketch, "E4.6.118.0", {"start": v(58.36, 19.3) * mm, "end": v(6.1, 1.75) * mm});
            skLineSegment(sketch, "E4.1.119.0", {"start": v(57.42, 21.95) * mm, "end": v(57.51, 21.7) * mm});
            skLineSegment(sketch, "E4.3.119.0", {"start": v(5.6, 2.99) * mm, "end": v(57.42, 21.95) * mm});
            skLineSegment(sketch, "E4.6.119.0", {"start": v(57.51, 21.7) * mm, "end": v(6.03, 2) * mm});
            skLineSegment(sketch, "E4.1.120.0", {"start": v(56.46, 24.3) * mm, "end": v(56.57, 24.05) * mm});
            skLineSegment(sketch, "E4.3.120.0", {"start": v(5.47, 3.22) * mm, "end": v(56.46, 24.3) * mm});
            skLineSegment(sketch, "E4.6.120.0", {"start": v(56.57, 24.05) * mm, "end": v(5.94, 2.24) * mm});
            skLineSegment(sketch, "E4.1.121.0", {"start": v(55.4, 26.62) * mm, "end": v(55.52, 26.37) * mm});
            skLineSegment(sketch, "E4.3.121.0", {"start": v(5.34, 3.44) * mm, "end": v(55.4, 26.62) * mm});
            skLineSegment(sketch, "E4.6.121.0", {"start": v(55.52, 26.37) * mm, "end": v(5.84, 2.49) * mm});
            skLineSegment(sketch, "E4.1.122.0", {"start": v(54.26, 28.88) * mm, "end": v(54.39, 28.64) * mm});
            skLineSegment(sketch, "E4.3.122.0", {"start": v(5.2, 3.66) * mm, "end": v(54.26, 28.88) * mm});
            skLineSegment(sketch, "E4.6.122.0", {"start": v(54.39, 28.64) * mm, "end": v(5.73, 2.73) * mm});
            skLineSegment(sketch, "E4.1.123.0", {"start": v(53.02, 31.1) * mm, "end": v(53.16, 30.87) * mm});
            skLineSegment(sketch, "E4.3.123.0", {"start": v(5.03, 3.87) * mm, "end": v(53.02, 31.1) * mm});
            skLineSegment(sketch, "E4.6.123.0", {"start": v(53.16, 30.87) * mm, "end": v(5.62, 2.96) * mm});
            skLineSegment(sketch, "E4.1.124.0", {"start": v(51.7, 33.27) * mm, "end": v(51.84, 33.04) * mm});
            skLineSegment(sketch, "E4.3.124.0", {"start": v(4.87, 4.07) * mm, "end": v(51.7, 33.27) * mm});
            skLineSegment(sketch, "E4.6.124.0", {"start": v(51.84, 33.04) * mm, "end": v(5.5, 3.2) * mm});
            skLineSegment(sketch, "E4.1.125.0", {"start": v(50.27, 35.37) * mm, "end": v(50.43, 35.15) * mm});
            skLineSegment(sketch, "E4.3.125.0", {"start": v(4.7, 4.27) * mm, "end": v(50.27, 35.37) * mm});
            skLineSegment(sketch, "E4.6.125.0", {"start": v(50.43, 35.15) * mm, "end": v(5.35, 3.41) * mm});
            skLineSegment(sketch, "E4.1.126.0", {"start": v(48.77, 37.42) * mm, "end": v(48.93, 37.2) * mm});
            skLineSegment(sketch, "E4.3.126.0", {"start": v(4.52, 4.46) * mm, "end": v(48.77, 37.42) * mm});
            skLineSegment(sketch, "E4.6.126.0", {"start": v(48.93, 37.2) * mm, "end": v(5.2, 3.63) * mm});
            skLineSegment(sketch, "E4.1.127.0", {"start": v(47.18, 39.4) * mm, "end": v(47.35, 39.2) * mm});
            skLineSegment(sketch, "E4.3.127.0", {"start": v(4.33, 4.65) * mm, "end": v(47.18, 39.4) * mm});
            skLineSegment(sketch, "E4.6.127.0", {"start": v(47.35, 39.2) * mm, "end": v(5.05, 3.85) * mm});
            skLineSegment(sketch, "E4.1.128.0", {"start": v(45.51, 41.32) * mm, "end": v(45.7, 41.12) * mm});
            skLineSegment(sketch, "E4.3.128.0", {"start": v(4.13, 4.82) * mm, "end": v(45.51, 41.32) * mm});
            skLineSegment(sketch, "E4.6.128.0", {"start": v(45.7, 41.12) * mm, "end": v(4.9, 4.05) * mm});
            skLineSegment(sketch, "E4.1.129.0", {"start": v(43.76, 43.17) * mm, "end": v(43.95, 42.97) * mm});
            skLineSegment(sketch, "E4.3.129.0", {"start": v(3.93, 4.99) * mm, "end": v(43.76, 43.17) * mm});
            skLineSegment(sketch, "E4.6.129.0", {"start": v(43.95, 42.97) * mm, "end": v(4.72, 4.25) * mm});
            skLineSegment(sketch, "E4.1.130.0", {"start": v(41.94, 44.94) * mm, "end": v(42.14, 44.75) * mm});
            skLineSegment(sketch, "E4.3.130.0", {"start": v(3.72, 5.15) * mm, "end": v(41.94, 44.94) * mm});
            skLineSegment(sketch, "E4.6.130.0", {"start": v(42.14, 44.75) * mm, "end": v(4.54, 4.44) * mm});
            skLineSegment(sketch, "E4.1.131.0", {"start": v(40.05, 46.63) * mm, "end": v(40.25, 46.45) * mm});
            skLineSegment(sketch, "E4.3.131.0", {"start": v(3.5, 5.3) * mm, "end": v(40.05, 46.63) * mm});
            skLineSegment(sketch, "E4.6.131.0", {"start": v(40.25, 46.45) * mm, "end": v(4.35, 4.62) * mm});
            skLineSegment(sketch, "E4.1.132.0", {"start": v(38.09, 48.25) * mm, "end": v(38.3, 48.08) * mm});
            skLineSegment(sketch, "E4.3.132.0", {"start": v(3.28, 5.44) * mm, "end": v(38.09, 48.25) * mm});
            skLineSegment(sketch, "E4.6.132.0", {"start": v(38.3, 48.08) * mm, "end": v(4.16, 4.8) * mm});
            skLineSegment(sketch, "E4.1.133.0", {"start": v(36.06, 49.78) * mm, "end": v(36.28, 49.62) * mm});
            skLineSegment(sketch, "E4.3.133.0", {"start": v(3.06, 5.57) * mm, "end": v(36.06, 49.78) * mm});
            skLineSegment(sketch, "E4.6.133.0", {"start": v(36.28, 49.62) * mm, "end": v(3.95, 4.97) * mm});
            skLineSegment(sketch, "E4.1.134.0", {"start": v(33.97, 51.23) * mm, "end": v(34.2, 51.08) * mm});
            skLineSegment(sketch, "E4.3.134.0", {"start": v(2.82, 5.69) * mm, "end": v(33.97, 51.23) * mm});
            skLineSegment(sketch, "E4.6.134.0", {"start": v(34.2, 51.08) * mm, "end": v(3.75, 5.13) * mm});
            skLineSegment(sketch, "E4.1.135.0", {"start": v(31.83, 52.59) * mm, "end": v(32.06, 52.44) * mm});
            skLineSegment(sketch, "E4.3.135.0", {"start": v(2.59, 5.8) * mm, "end": v(31.83, 52.59) * mm});
            skLineSegment(sketch, "E4.6.135.0", {"start": v(32.06, 52.44) * mm, "end": v(3.53, 5.28) * mm});
            skLineSegment(sketch, "E4.1.136.0", {"start": v(29.63, 53.86) * mm, "end": v(29.87, 53.72) * mm});
            skLineSegment(sketch, "E4.3.136.0", {"start": v(2.34, 5.9) * mm, "end": v(29.63, 53.86) * mm});
            skLineSegment(sketch, "E4.6.136.0", {"start": v(29.87, 53.72) * mm, "end": v(3.3, 5.42) * mm});
            skLineSegment(sketch, "E4.1.137.0", {"start": v(27.38, 55.04) * mm, "end": v(27.62, 54.91) * mm});
            skLineSegment(sketch, "E4.3.137.0", {"start": v(2.1, 6) * mm, "end": v(27.38, 55.04) * mm});
            skLineSegment(sketch, "E4.6.137.0", {"start": v(27.62, 54.91) * mm, "end": v(3.08, 5.55) * mm});
            skLineSegment(sketch, "E4.1.138.0", {"start": v(25.08, 56.12) * mm, "end": v(25.33, 56) * mm});
            skLineSegment(sketch, "E4.3.138.0", {"start": v(1.85, 6.08) * mm, "end": v(25.08, 56.12) * mm});
            skLineSegment(sketch, "E4.6.138.0", {"start": v(25.33, 56) * mm, "end": v(2.85, 5.67) * mm});
            skLineSegment(sketch, "E4.1.139.0", {"start": v(22.74, 57.11) * mm, "end": v(23, 57) * mm});
            skLineSegment(sketch, "E4.3.139.0", {"start": v(1.6, 6.15) * mm, "end": v(22.74, 57.11) * mm});
            skLineSegment(sketch, "E4.6.139.0", {"start": v(23, 57) * mm, "end": v(2.61, 5.79) * mm});
            skLineSegment(sketch, "E4.1.140.0", {"start": v(20.36, 58) * mm, "end": v(20.61, 57.9) * mm});
            skLineSegment(sketch, "E4.3.140.0", {"start": v(1.34, 6.2) * mm, "end": v(20.36, 58) * mm});
            skLineSegment(sketch, "E4.6.140.0", {"start": v(20.61, 57.9) * mm, "end": v(2.37, 5.9) * mm});
            skLineSegment(sketch, "E4.1.141.0", {"start": v(17.95, 58.8) * mm, "end": v(18.2, 58.71) * mm});
            skLineSegment(sketch, "E4.3.141.0", {"start": v(1.08, 6.26) * mm, "end": v(17.95, 58.8) * mm});
            skLineSegment(sketch, "E4.6.141.0", {"start": v(18.2, 58.71) * mm, "end": v(2.13, 5.98) * mm});
            skLineSegment(sketch, "E4.1.142.0", {"start": v(15.5, 59.48) * mm, "end": v(15.76, 59.41) * mm});
            skLineSegment(sketch, "E4.3.142.0", {"start": v(0.82, 6.3) * mm, "end": v(15.5, 59.48) * mm});
            skLineSegment(sketch, "E4.6.142.0", {"start": v(15.76, 59.41) * mm, "end": v(1.88, 6.07) * mm});
            skLineSegment(sketch, "E4.1.143.0", {"start": v(13.03, 60.07) * mm, "end": v(13.3, 60.01) * mm});
            skLineSegment(sketch, "E4.3.143.0", {"start": v(0.56, 6.33) * mm, "end": v(13.03, 60.07) * mm});
            skLineSegment(sketch, "E4.6.143.0", {"start": v(13.3, 60.01) * mm, "end": v(1.63, 6.14) * mm});
            skLineSegment(sketch, "E4.1.144.0", {"start": v(10.53, 60.56) * mm, "end": v(10.8, 60.51) * mm});
            skLineSegment(sketch, "E4.3.144.0", {"start": v(0.3, 6.34) * mm, "end": v(10.53, 60.56) * mm});
            skLineSegment(sketch, "E4.6.144.0", {"start": v(10.8, 60.51) * mm, "end": v(1.37, 6.2) * mm});
            skLineSegment(sketch, "E4.1.145.0", {"start": v(8.02, 60.95) * mm, "end": v(8.3, 60.9) * mm});
            skLineSegment(sketch, "E4.3.145.0", {"start": v(0.04, 6.35) * mm, "end": v(8.02, 60.95) * mm});
            skLineSegment(sketch, "E4.6.145.0", {"start": v(8.3, 60.9) * mm, "end": v(1.11, 6.25) * mm});
            skLineSegment(sketch, "E4.1.146.0", {"start": v(5.5, 61.22) * mm, "end": v(5.77, 61.2) * mm});
            skLineSegment(sketch, "E4.3.146.0", {"start": v(-0.22, 6.35) * mm, "end": v(5.5, 61.22) * mm});
            skLineSegment(sketch, "E4.6.146.0", {"start": v(5.77, 61.2) * mm, "end": v(0.85, 6.3) * mm});
            skLineSegment(sketch, "E4.1.147.0", {"start": v(2.96, 61.4) * mm, "end": v(3.23, 61.38) * mm});
            skLineSegment(sketch, "E4.3.147.0", {"start": v(-0.49, 6.33) * mm, "end": v(2.96, 61.4) * mm});
            skLineSegment(sketch, "E4.6.147.0", {"start": v(3.23, 61.38) * mm, "end": v(0.6, 6.32) * mm});
            skLineSegment(sketch, "E4.1.148.0", {"start": v(0.42, 61.47) * mm, "end": v(0.7, 61.46) * mm});
            skLineSegment(sketch, "E4.3.148.0", {"start": v(-0.75, 6.3) * mm, "end": v(0.42, 61.47) * mm});
            skLineSegment(sketch, "E4.6.148.0", {"start": v(0.7, 61.46) * mm, "end": v(0.33, 6.34) * mm});
            skLineSegment(sketch, "E4.1.149.0", {"start": v(-2.12, 61.43) * mm, "end": v(-1.85, 61.44) * mm});
            skLineSegment(sketch, "E4.3.149.0", {"start": v(-1, 6.27) * mm, "end": v(-2.12, 61.43) * mm});
            skLineSegment(sketch, "E4.6.149.0", {"start": v(-1.85, 61.44) * mm, "end": v(0.07, 6.35) * mm});
            skLineSegment(sketch, "E5.1.150.0", {"start": v(-4.65, 61.3) * mm, "end": v(-4.38, 61.31) * mm});
            skLineSegment(sketch, "E5.3.150.0", {"start": v(-1.27, 6.22) * mm, "end": v(-4.65, 61.3) * mm});
            skLineSegment(sketch, "E5.6.150.0", {"start": v(-4.38, 61.31) * mm, "end": v(-0.2, 6.35) * mm});
            skLineSegment(sketch, "E5.1.151.0", {"start": v(-7.18, 61.05) * mm, "end": v(-6.91, 61.08) * mm});
            skLineSegment(sketch, "E5.3.151.0", {"start": v(-1.52, 6.16) * mm, "end": v(-7.18, 61.05) * mm});
            skLineSegment(sketch, "E5.6.151.0", {"start": v(-6.91, 61.08) * mm, "end": v(-0.46, 6.33) * mm});
            skLineSegment(sketch, "E6.1.0", {"start": v(-4.4, -4.59) * mm, "end": v(-47.72, -38.75) * mm});
            skLineSegment(sketch, "E6.1.1", {"start": v(-47.89, -38.54) * mm, "end": v(-5.1, -3.78) * mm});
            skLineSegment(sketch, "E6.1.2", {"start": v(-47.72, -38.75) * mm, "end": v(-47.89, -38.54) * mm});
            skLineSegment(sketch, "E6.2.0", {"start": v(6.17, -1.51) * mm, "end": v(57.42, -21.95) * mm});
            skLineSegment(sketch, "E6.2.1", {"start": v(57.32, -22.2) * mm, "end": v(5.82, -2.53) * mm});
            skLineSegment(sketch, "E6.2.2", {"start": v(57.42, -21.95) * mm, "end": v(57.32, -22.2) * mm});
            skCircle(sketch, "E7", {"center": v(-9.7, 60.7) * mm, "radius": 0.3 * mm});
            skCircle(sketch, "E8", {"center": v(-9.43, 60.74) * mm, "radius": 0.31 * mm});
            skLineSegment(sketch, "E9", {"start": v(-9.81, 60.99) * mm, "end": v(-10.08, 61.86) * mm});
            skLineSegment(sketch, "E10", {"start": v(-10.08, 61.86) * mm, "end": v(-10.07, 62.26) * mm});
            skLineSegment(sketch, "E11", {"start": v(-10.07, 62.26) * mm, "end": v(-9.95, 62.3) * mm});
            skLineSegment(sketch, "E12", {"start": v(-9.95, 62.3) * mm, "end": v(-9.7, 62) * mm});
            skSolve(sketch);
        }
        {
            var Q0;
            Q0 = qSketchRegion(id + "F0", true);
            extrude(context, id + "F1", {"entities" : qUnion([Q0]), "depth" : 25.4 * mm});
        }
        {
            var Q0;
            Q0 = qSketchRegion(id + "F0", true);
            extrude(context, id + "F2", {"entities" : qUnion([Q0]), "operationType" : NewBodyOperationType.ADD, "depth" : 25.4 * mm});
        }
    });
